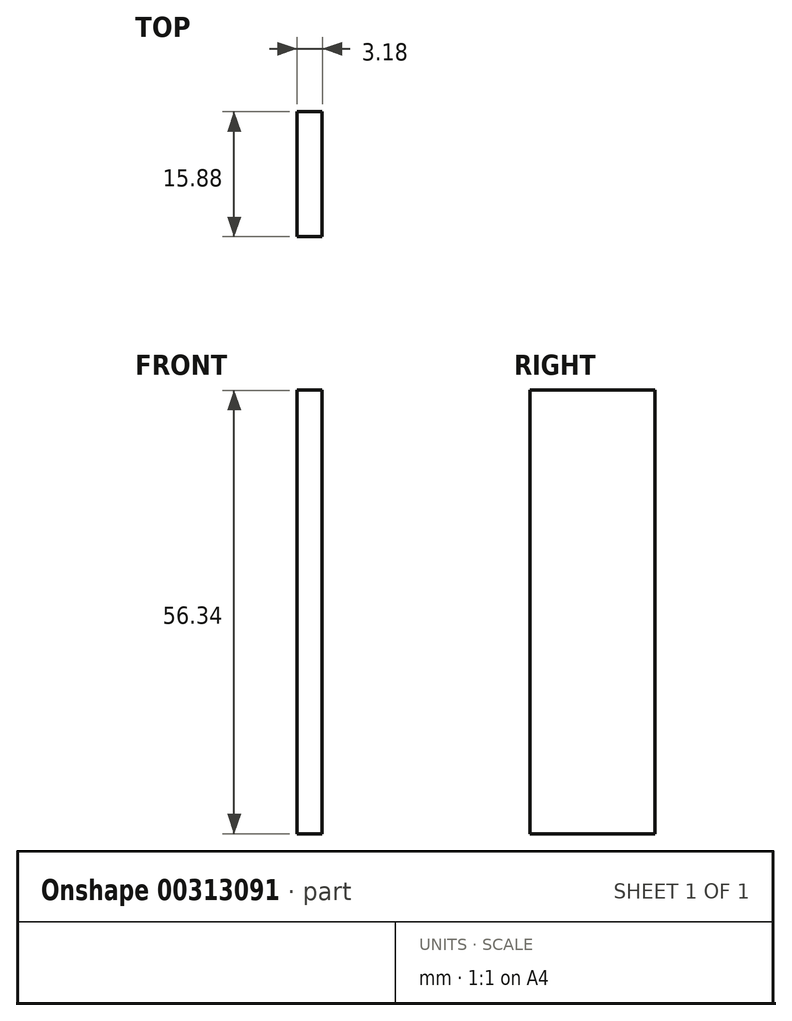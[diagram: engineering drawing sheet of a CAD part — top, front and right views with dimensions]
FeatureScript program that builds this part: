
annotation { "Feature Type Name" : "Feature", "Feature Type Description" : "" }
export const myFeature = defineFeature(function(context is Context, id is Id, definition is map)
    precondition{}
    {
        {
            var Q0;
            Q0=qCreatedBy(makeId("Top.planeOp"),FACE);
            var sketch = newSketch(context, id + "F0", { "sketchPlane" : qUnion([Q0])});
            skLineSegment(sketch, "E0.bottom", {"start": v(1.59, -7.94) * mm, "end": v(-1.59, -7.94) * mm});
            skLineSegment(sketch, "E0.top", {"start": v(1.59, 7.94) * mm, "end": v(-1.59, 7.94) * mm});
            skLineSegment(sketch, "E0.left", {"start": v(1.59, -7.94) * mm, "end": v(1.59, 7.94) * mm});
            skLineSegment(sketch, "E0.right", {"start": v(-1.59, -7.94) * mm, "end": v(-1.59, 7.94) * mm});
            skPoint(sketch, "E0.middle", {"position": v(0, 0) * mm});
            skSolve(sketch);
        }
        {
            var Q0;
            Q0 = qSketchRegion(id + "F0", true);
            extrude(context, id + "F1", {"entities" : qUnion([Q0]), "endBound" : BoundingType.SYMMETRIC, "depth" : 56.35 * mm});
        }
    });
